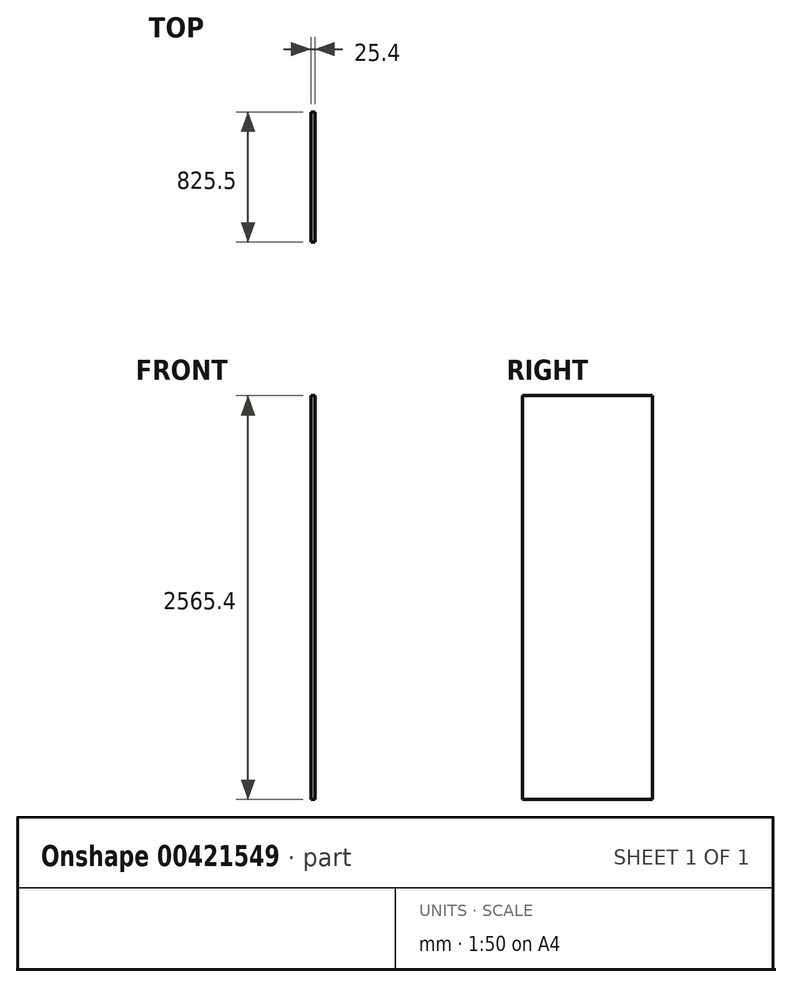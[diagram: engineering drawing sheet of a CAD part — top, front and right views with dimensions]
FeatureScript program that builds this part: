
annotation { "Feature Type Name" : "Feature", "Feature Type Description" : "" }
export const myFeature = defineFeature(function(context is Context, id is Id, definition is map)
    precondition{}
    {
        {
            var Q0;
            Q0=qCreatedBy(makeId("Right.planeOp"),FACE);
            var sketch = newSketch(context, id + "F0", { "sketchPlane" : qUnion([Q0])});
            skLineSegment(sketch, "E0.bottom", {"start": v(0, 0) * mm, "end": v(825.5, 0) * mm});
            skLineSegment(sketch, "E0.top", {"start": v(0, 2565.4) * mm, "end": v(825.5, 2565.4) * mm});
            skLineSegment(sketch, "E0.left", {"start": v(0, 0) * mm, "end": v(0, 2565.4) * mm});
            skLineSegment(sketch, "E0.right", {"start": v(825.5, 0) * mm, "end": v(825.5, 2565.4) * mm});
            skSolve(sketch);
        }
        {
            var Q0;
            Q0 = qSketchRegion(id + "F0", true);
            extrude(context, id + "F1", {"entities" : qUnion([Q0]), "depth" : 25.4 * mm});
        }
    });
